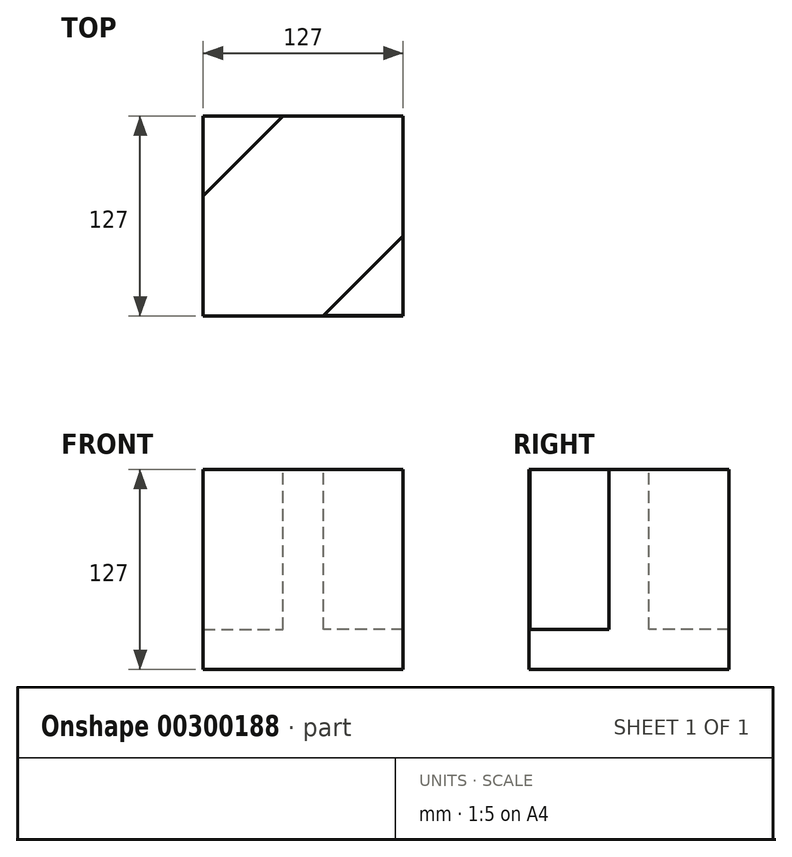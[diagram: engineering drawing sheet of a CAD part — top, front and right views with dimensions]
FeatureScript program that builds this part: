
annotation { "Feature Type Name" : "Feature", "Feature Type Description" : "" }
export const myFeature = defineFeature(function(context is Context, id is Id, definition is map)
    precondition{}
    {
        {
            var Q0;
            Q0=qCreatedBy(makeId("Top.planeOp"),FACE);
            var sketch = newSketch(context, id + "F0", { "sketchPlane" : qUnion([Q0])});
            skLineSegment(sketch, "E0", {"start": v(-63.57, 64.12) * mm, "end": v(-63.57, -62.88) * mm});
            skLineSegment(sketch, "E1", {"start": v(-63.57, -62.88) * mm, "end": v(63.43, -62.88) * mm});
            skLineSegment(sketch, "E2", {"start": v(63.43, -62.88) * mm, "end": v(63.43, 64.12) * mm});
            skLineSegment(sketch, "E3", {"start": v(63.43, 64.12) * mm, "end": v(-63.57, 64.12) * mm});
            skSolve(sketch);
        }
        {
            var Q0;
            Q0=qCreatedBy(makeId("Top.planeOp"),FACE);
            var sketch = newSketch(context, id + "F1", { "sketchPlane" : qUnion([Q0])});
            skLineSegment(sketch, "E4", {"start": v(-63.56, 64.1) * mm, "end": v(-63.56, 13.3) * mm});
            skLineSegment(sketch, "E5", {"start": v(-63.56, 64.1) * mm, "end": v(-12.76, 64.1) * mm});
            skLineSegment(sketch, "E6", {"start": v(-12.76, 64.1) * mm, "end": v(-63.56, 13.3) * mm});
            skSolve(sketch);
        }
        {
            var Q0;
            Q0=qCreatedBy(makeId("Top.planeOp"),FACE);
            var sketch = newSketch(context, id + "F2", { "sketchPlane" : qUnion([Q0])});
            skLineSegment(sketch, "E7", {"start": v(63.77, -62.51) * mm, "end": v(63.77, -11.71) * mm});
            skLineSegment(sketch, "E8", {"start": v(63.77, -62.51) * mm, "end": v(12.97, -62.51) * mm});
            skLineSegment(sketch, "E9", {"start": v(12.97, -62.51) * mm, "end": v(63.77, -11.71) * mm});
            skSolve(sketch);
        }
        {
            var Q0;
            Q0=makeQuery(id+"F0.imprint","IMPRINT",FACE,{"disambiguationData":[TD([[makeQuery(id+"F0.imprint","IMPRINT",EDGE,{"derivedFrom":sQuery(id+"F0.wireOp",EDGE,"E0")}),1.0]])]});
            extrude(context, id + "F3", {"entities" : qUnion([Q0]), "oppositeDirection" : true, "depth" : 127 * mm});
        }
        {
            var Q0;
            Q0=makeQuery(id+"F2.imprint","IMPRINT",FACE,{"disambiguationData":[TD([[makeQuery(id+"F2.imprint","IMPRINT",EDGE,{"derivedFrom":sQuery(id+"F2.wireOp",EDGE,"E7")}),1.0]])]});
            var Q1;
            Q1=makeQuery(id+"F1.imprint","IMPRINT",FACE,{"disambiguationData":[TD([[makeQuery(id+"F1.imprint","IMPRINT",EDGE,{"derivedFrom":sQuery(id+"F1.wireOp",EDGE,"E4")}),1.0]])]});
            extrude(context, id + "F4", {"entities" : qUnion([Q0, Q1]), "operationType" : NewBodyOperationType.REMOVE, "oppositeDirection" : true, "depth" : 101.6 * mm});
        }
    });
